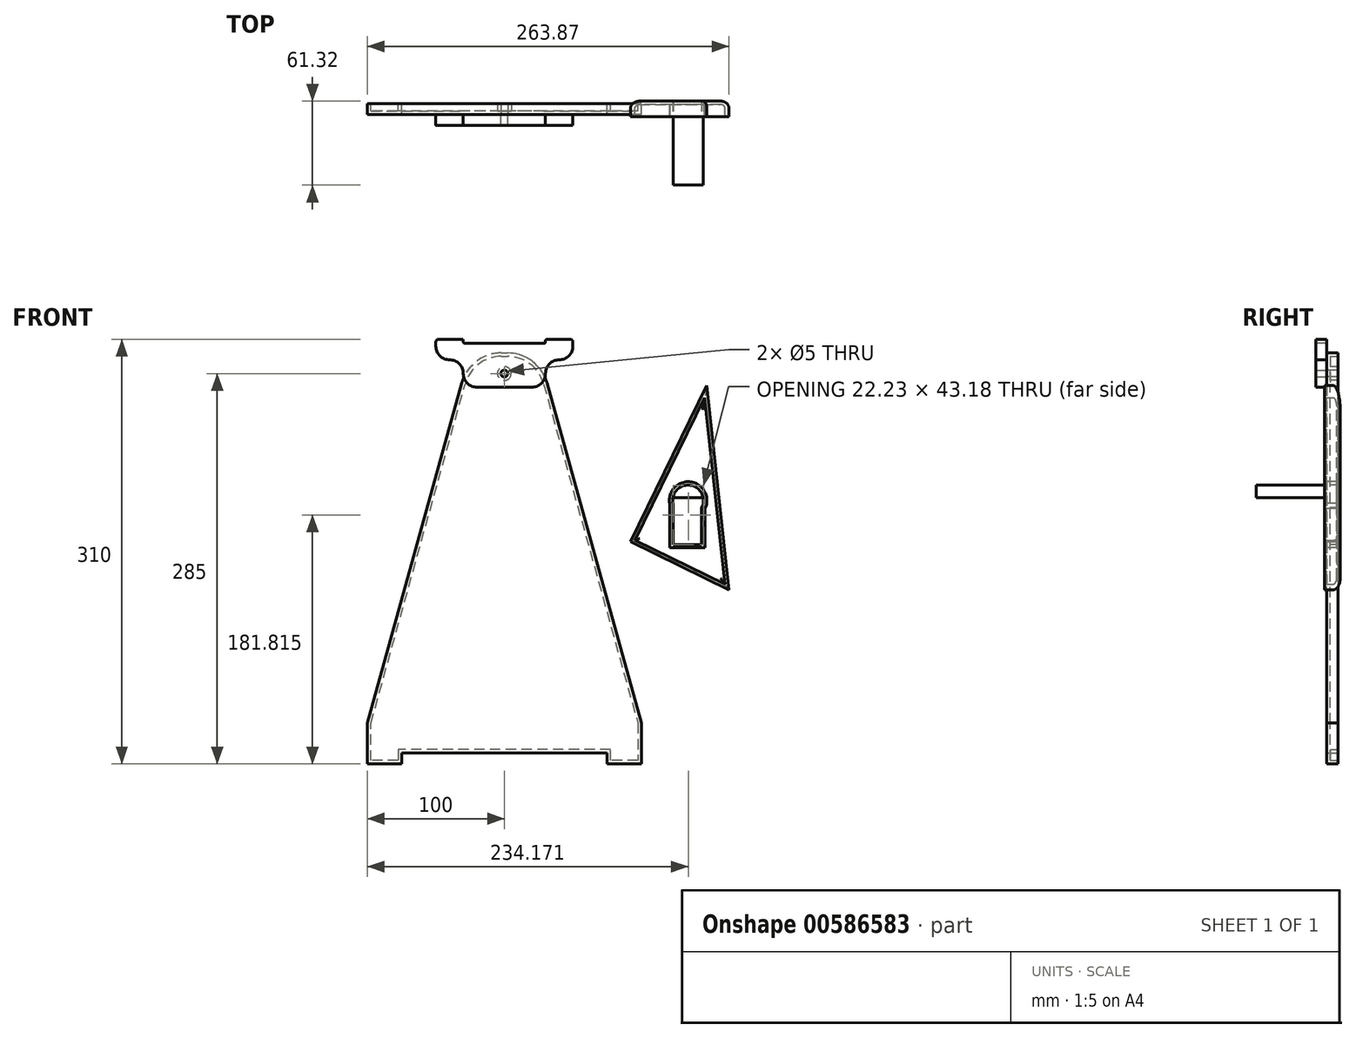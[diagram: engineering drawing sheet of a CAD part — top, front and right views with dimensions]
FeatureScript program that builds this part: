
annotation { "Feature Type Name" : "Feature", "Feature Type Description" : "" }
export const myFeature = defineFeature(function(context is Context, id is Id, definition is map)
    precondition{}
    {
        {
            var Q0;
            Q0=qCreatedBy(makeId("Front.planeOp"),FACE);
            var sketch = newSketch(context, id + "F0", { "sketchPlane" : qUnion([Q0])});
            skLineSegment(sketch, "E0", {"start": v(-25, 0) * mm, "end": v(25, 0) * mm});
            skLineSegment(sketch, "E1", {"start": v(25, 0) * mm, "end": v(100, -270) * mm});
            skLineSegment(sketch, "E2", {"start": v(100, -270) * mm, "end": v(100, -300) * mm});
            skLineSegment(sketch, "E3", {"start": v(100, -300) * mm, "end": v(75, -300) * mm});
            skLineSegment(sketch, "E4", {"start": v(75, -300) * mm, "end": v(75, -292) * mm});
            skLineSegment(sketch, "E5", {"start": v(75, -292) * mm, "end": v(-75, -292) * mm});
            skLineSegment(sketch, "E6", {"start": v(-75, -292) * mm, "end": v(-75, -300) * mm});
            skLineSegment(sketch, "E7", {"start": v(-75, -300) * mm, "end": v(-100, -300) * mm});
            skLineSegment(sketch, "E8", {"start": v(-100, -300) * mm, "end": v(-100, -270) * mm});
            skLineSegment(sketch, "E9", {"start": v(-100, -270) * mm, "end": v(-25, 0) * mm});
            skSolve(sketch);
        }
        {
            var Q0;
            Q0=makeQuery(id+"F0.imprint","IMPRINT",FACE,{"disambiguationData":[TD([[makeQuery(id+"F0.imprint","IMPRINT",EDGE,{"derivedFrom":sQuery(id+"F0.wireOp",EDGE,"E0")}),-1.0]])]});
            extrude(context, id + "F1", {"entities" : qUnion([Q0]), "endBound" : BoundingType.SYMMETRIC, "depth" : 8 * mm, "offsetDistance" : 25 * mm});
        }
        {
            var Q0;
            Q0=makeQuery(id+"F1.opExtrude","SWEPT_EDGE",EDGE,{"disambiguationData":[OSD([sQuery(id+"F0.wireOp",EDGE,"E0"),sQuery(id+"F0.wireOp",EDGE,"E9")])]});
            var Q1;
            Q1=makeQuery(id+"F1.opExtrude","SWEPT_EDGE",EDGE,{"disambiguationData":[OSD([sQuery(id+"F0.wireOp",EDGE,"E0"),sQuery(id+"F0.wireOp",EDGE,"E1")])]});
            fillet(context, id + "F2", {"entities" : qUnion([Q0, Q1]), "radius" : 30 * mm, "tangentPropagation" : true, "allowEdgeOverflow" : false});
        }
        {
            var Q0;
            Q0=makeQuery(id+"F1.opExtrude","CAP_FACE",FACE,{"disambiguationData":[OSD([sQuery(id+"F0.wireOp",EDGE,"E0"),sQuery(id+"F0.wireOp",EDGE,"E1"),sQuery(id+"F0.wireOp",EDGE,"E2"),sQuery(id+"F0.wireOp",EDGE,"E3"),sQuery(id+"F0.wireOp",EDGE,"E4"),sQuery(id+"F0.wireOp",EDGE,"E5"),sQuery(id+"F0.wireOp",EDGE,"E6"),sQuery(id+"F0.wireOp",EDGE,"E7"),sQuery(id+"F0.wireOp",EDGE,"E8"),sQuery(id+"F0.wireOp",EDGE,"E9")])],"isStart":false});
            var sketch = newSketch(context, id + "F3", { "sketchPlane" : qUnion([Q0])});
            skCircle(sketch, "E10", {"center": v(0, -15) * mm, "radius": 2.5 * mm});
            skSolve(sketch);
        }
        {
            var Q0;
            Q0=makeQuery(id+"F3.imprint","IMPRINT",FACE,{"disambiguationData":[TD([[makeQuery(id+"F3.imprint","IMPRINT",EDGE,{"derivedFrom":sQuery(id+"F3.wireOp",EDGE,"E10")}),1.0]])]});
            extrude(context, id + "F4", {"entities" : qUnion([Q0]), "operationType" : NewBodyOperationType.REMOVE, "endBound" : BoundingType.THROUGH_ALL, "oppositeDirection" : true, "depth" : 25 * mm, "offsetDistance" : 25 * mm});
        }
        {
            var Q0;
            Q0=makeQuery(id+"F1.opExtrude","CAP_FACE",FACE,{"disambiguationData":[OSD([sQuery(id+"F0.wireOp",EDGE,"E0"),sQuery(id+"F0.wireOp",EDGE,"E1"),sQuery(id+"F0.wireOp",EDGE,"E2"),sQuery(id+"F0.wireOp",EDGE,"E3"),sQuery(id+"F0.wireOp",EDGE,"E4"),sQuery(id+"F0.wireOp",EDGE,"E5"),sQuery(id+"F0.wireOp",EDGE,"E6"),sQuery(id+"F0.wireOp",EDGE,"E7"),sQuery(id+"F0.wireOp",EDGE,"E8"),sQuery(id+"F0.wireOp",EDGE,"E9")])],"isStart":false});
            var sketch = newSketch(context, id + "F5", { "sketchPlane" : qUnion([Q0])});
            skLineSegment(sketch, "E11", {"start": v(-50, 10) * mm, "end": v(50, 10) * mm});
            skLineSegment(sketch, "E12", {"start": v(50, 10) * mm, "end": v(50, -5) * mm});
            skLineSegment(sketch, "E13", {"start": v(50, -5) * mm, "end": v(30, -5) * mm});
            skLineSegment(sketch, "E14", {"start": v(30, -5) * mm, "end": v(30, -25) * mm});
            skLineSegment(sketch, "E15", {"start": v(30, -25) * mm, "end": v(-30, -25) * mm});
            skLineSegment(sketch, "E16", {"start": v(-30, -25) * mm, "end": v(-30, -5) * mm});
            skLineSegment(sketch, "E17", {"start": v(-30, -5) * mm, "end": v(-50, -5) * mm});
            skLineSegment(sketch, "E18", {"start": v(-50, -5) * mm, "end": v(-50, 10) * mm});
            skSolve(sketch);
        }
        {
            var Q0;
            Q0 = qSketchRegion(id + "F5", true);
            extrude(context, id + "F6", {"entities" : qUnion([Q0]), "depth" : 8 * mm, "offsetDistance" : 25 * mm});
        }
        {
            var Q0;
            Q0=makeQuery(id+"F6.opExtrude","SWEPT_EDGE",EDGE,{"disambiguationData":[OSD([sQuery(id+"F5.wireOp",EDGE,"E11"),sQuery(id+"F5.wireOp",EDGE,"E18")])]});
            var Q1;
            Q1=makeQuery(id+"F6.opExtrude","SWEPT_EDGE",EDGE,{"disambiguationData":[OSD([sQuery(id+"F5.wireOp",EDGE,"E11"),sQuery(id+"F5.wireOp",EDGE,"E12")])]});
            fillet(context, id + "F7", {"entities" : qUnion([Q0, Q1]), "radius" : 2 * mm, "tangentPropagation" : true, "allowEdgeOverflow" : false});
        }
        {
            var Q0;
            Q0=makeQuery(id+"F6.opExtrude","SWEPT_EDGE",EDGE,{"disambiguationData":[OSD([sQuery(id+"F5.wireOp",EDGE,"E13"),sQuery(id+"F5.wireOp",EDGE,"E14")])]});
            var Q1;
            Q1=makeQuery(id+"F6.opExtrude","SWEPT_EDGE",EDGE,{"disambiguationData":[OSD([sQuery(id+"F5.wireOp",EDGE,"E14"),sQuery(id+"F5.wireOp",EDGE,"E15")])]});
            var Q2;
            Q2=makeQuery(id+"F6.opExtrude","SWEPT_EDGE",EDGE,{"disambiguationData":[OSD([sQuery(id+"F5.wireOp",EDGE,"E15"),sQuery(id+"F5.wireOp",EDGE,"E16")])]});
            var Q3;
            Q3=makeQuery(id+"F6.opExtrude","SWEPT_EDGE",EDGE,{"disambiguationData":[OSD([sQuery(id+"F5.wireOp",EDGE,"E16"),sQuery(id+"F5.wireOp",EDGE,"E17")])]});
            var Q4;
            Q4=makeQuery(id+"F6.opExtrude","SWEPT_EDGE",EDGE,{"disambiguationData":[OSD([sQuery(id+"F5.wireOp",EDGE,"E17"),sQuery(id+"F5.wireOp",EDGE,"E18")])]});
            var Q5;
            Q5=makeQuery(id+"F6.opExtrude","SWEPT_EDGE",EDGE,{"disambiguationData":[OSD([sQuery(id+"F5.wireOp",EDGE,"E12"),sQuery(id+"F5.wireOp",EDGE,"E13")])]});
            fillet(context, id + "F8", {"entities" : qUnion([Q0, Q1, Q2, Q3, Q4, Q5]), "radius" : 10 * mm, "tangentPropagation" : true, "allowEdgeOverflow" : false});
        }
        {
            var Q0;
            Q0=makeQuery(id+"F6.opExtrude","CAP_FACE",FACE,{"disambiguationData":[OSD([sQuery(id+"F5.wireOp",EDGE,"E11"),sQuery(id+"F5.wireOp",EDGE,"E12"),sQuery(id+"F5.wireOp",EDGE,"E13"),sQuery(id+"F5.wireOp",EDGE,"E14"),sQuery(id+"F5.wireOp",EDGE,"E15"),sQuery(id+"F5.wireOp",EDGE,"E16"),sQuery(id+"F5.wireOp",EDGE,"E17"),sQuery(id+"F5.wireOp",EDGE,"E18")])],"isStart":false});
            var sketch = newSketch(context, id + "F9", { "sketchPlane" : qUnion([Q0])});
            skLineSegment(sketch, "E19.bottom", {"start": v(-30, 10) * mm, "end": v(30, 10) * mm});
            skLineSegment(sketch, "E19.top", {"start": v(-30, 7) * mm, "end": v(30, 7) * mm});
            skLineSegment(sketch, "E19.left", {"start": v(-30, 10) * mm, "end": v(-30, 7) * mm});
            skLineSegment(sketch, "E19.right", {"start": v(30, 10) * mm, "end": v(30, 7) * mm});
            skSolve(sketch);
        }
        {
            var Q0;
            Q0=makeQuery(id+"F9.imprint","IMPRINT",FACE,{"disambiguationData":[TD([[makeQuery(id+"F9.imprint","IMPRINT",EDGE,{"derivedFrom":sQuery(id+"F9.wireOp",EDGE,"E19.bottom")}),-1.0]])]});
            extrude(context, id + "F10", {"entities" : qUnion([Q0]), "operationType" : NewBodyOperationType.REMOVE, "endBound" : BoundingType.UP_TO_NEXT, "oppositeDirection" : true, "depth" : 25 * mm, "offsetDistance" : 25 * mm});
        }
        {
            var Q0;
            Q0=makeQuery(id+"F10.boolean.opBoolean","COPY",EDGE,{"derivedFrom":makeQuery(id+"F10.opExtrude","SWEPT_EDGE",EDGE,{"disambiguationData":[OSD([sQuery(id+"F5.wireOp",EDGE,"E11"),sQuery(id+"F9.wireOp",EDGE,"E19.bottom"),sQuery(id+"F9.wireOp",EDGE,"E19.left")])]})});
            var Q1;
            Q1=makeQuery(id+"F10.boolean.opBoolean","COPY",EDGE,{"derivedFrom":makeQuery(id+"F10.opExtrude","SWEPT_EDGE",EDGE,{"disambiguationData":[OSD([sQuery(id+"F9.wireOp",EDGE,"E19.top"),sQuery(id+"F9.wireOp",EDGE,"E19.left")])]})});
            var Q2;
            Q2=makeQuery(id+"F10.boolean.opBoolean","COPY",EDGE,{"derivedFrom":makeQuery(id+"F10.opExtrude","SWEPT_EDGE",EDGE,{"disambiguationData":[OSD([sQuery(id+"F5.wireOp",EDGE,"E11"),sQuery(id+"F9.wireOp",EDGE,"E19.bottom"),sQuery(id+"F9.wireOp",EDGE,"E19.right")])]})});
            var Q3;
            Q3=makeQuery(id+"F10.boolean.opBoolean","COPY",EDGE,{"derivedFrom":makeQuery(id+"F10.opExtrude","SWEPT_EDGE",EDGE,{"disambiguationData":[OSD([sQuery(id+"F9.wireOp",EDGE,"E19.top"),sQuery(id+"F9.wireOp",EDGE,"E19.right")])]})});
            fillet(context, id + "F11", {"entities" : qUnion([Q0, Q1, Q2, Q3]), "radius" : 1 * mm, "tangentPropagation" : true, "allowEdgeOverflow" : false});
        }
        {
            var Q0;
            Q0=makeQuery(id+"F6.opExtrude","CAP_FACE",FACE,{"disambiguationData":[OSD([sQuery(id+"F5.wireOp",EDGE,"E11"),sQuery(id+"F5.wireOp",EDGE,"E12"),sQuery(id+"F5.wireOp",EDGE,"E13"),sQuery(id+"F5.wireOp",EDGE,"E14"),sQuery(id+"F5.wireOp",EDGE,"E15"),sQuery(id+"F5.wireOp",EDGE,"E16"),sQuery(id+"F5.wireOp",EDGE,"E17"),sQuery(id+"F5.wireOp",EDGE,"E18")])],"isStart":true});
            var sketch = newSketch(context, id + "F12", { "sketchPlane" : qUnion([Q0])});
            skCircle(sketch, "E20.0", {"center": v(0, -15) * mm, "radius": 2.5 * mm});
            skSolve(sketch);
        }
        {
            var Q0;
            Q0 = qSketchRegion(id + "F12", true);
            extrude(context, id + "F13", {"entities" : qUnion([Q0]), "operationType" : NewBodyOperationType.REMOVE, "endBound" : BoundingType.UP_TO_NEXT, "oppositeDirection" : true, "depth" : 25 * mm, "offsetDistance" : 25 * mm});
        }
        {
            var Q0;
            Q0=qCreatedBy(makeId("Front.planeOp"),FACE);
            var sketch = newSketch(context, id + "F14", { "sketchPlane" : qUnion([Q0])});
            skLineSegment(sketch, "E21", {"start": v(92, -137.78) * mm, "end": v(147.78, -23.81) * mm});
            skLineSegment(sketch, "E22", {"start": v(147.78, -23.81) * mm, "end": v(163.87, -172.95) * mm});
            skLineSegment(sketch, "E23", {"start": v(163.87, -172.95) * mm, "end": v(92, -137.78) * mm});
            skSolve(sketch);
        }
        {
            var Q0;
            Q0=makeQuery(id+"F14.imprint","IMPRINT",FACE,{"disambiguationData":[TD([[makeQuery(id+"F14.imprint","IMPRINT",EDGE,{"derivedFrom":sQuery(id+"F14.wireOp",EDGE,"E21")}),-1.0]])]});
            extrude(context, id + "F15", {"entities" : qUnion([Q0]), "endBound" : BoundingType.SYMMETRIC, "depth" : 11.32 * mm, "offsetDistance" : 25 * mm});
        }
        {
            var Q0;
            Q0=makeQuery(id+"F15.opExtrude","CAP_FACE",FACE,{"disambiguationData":[OSD([sQuery(id+"F14.wireOp",EDGE,"E21"),sQuery(id+"F14.wireOp",EDGE,"E22"),sQuery(id+"F14.wireOp",EDGE,"E23")])],"isStart":false});
            var sketch = newSketch(context, id + "F16", { "sketchPlane" : qUnion([Q0])});
            skCircle(sketch, "E24", {"center": v(134.08, -107.67) * mm, "radius": 11.2 * mm});
            skLineSegment(sketch, "E25.bottom", {"start": v(123.06, -109.68) * mm, "end": v(144, -109.68) * mm});
            skLineSegment(sketch, "E25.top", {"start": v(123.06, -139.77) * mm, "end": v(144, -139.77) * mm});
            skLineSegment(sketch, "E25.left", {"start": v(123.06, -109.68) * mm, "end": v(123.06, -139.77) * mm});
            skLineSegment(sketch, "E25.right", {"start": v(144, -109.68) * mm, "end": v(144, -139.77) * mm});
            skSolve(sketch);
        }
        {
            var Q0;
            Q0 = qSketchRegion(id + "F16", true);
            extrude(context, id + "F17", {"entities" : qUnion([Q0]), "operationType" : NewBodyOperationType.REMOVE, "endBound" : BoundingType.THROUGH_ALL, "oppositeDirection" : true, "depth" : 25 * mm, "offsetDistance" : 25 * mm});
        }
        {
            var Q0;
            Q0=makeQuery(id+"F15.opExtrude","CAP_EDGE",EDGE,{"disambiguationData":[OSD([sQuery(id+"F14.wireOp",EDGE,"E22")])],"isStart":true});
            var Q1;
            Q1=makeQuery(id+"F15.opExtrude","CAP_EDGE",EDGE,{"disambiguationData":[OSD([sQuery(id+"F14.wireOp",EDGE,"E23")])],"isStart":true});
            var Q2;
            Q2=makeQuery(id+"F15.opExtrude","CAP_EDGE",EDGE,{"disambiguationData":[OSD([sQuery(id+"F14.wireOp",EDGE,"E21")])],"isStart":true});
            fillet(context, id + "F18", {"entities" : qUnion([Q0, Q1, Q2]), "radius" : 5 * mm, "tangentPropagation" : true, "allowEdgeOverflow" : false});
        }
        {
            var Q0;
            Q0=makeQuery(id+"F15.opExtrude","CAP_FACE",FACE,{"disambiguationData":[OSD([sQuery(id+"F14.wireOp",EDGE,"E21"),sQuery(id+"F14.wireOp",EDGE,"E22"),sQuery(id+"F14.wireOp",EDGE,"E23")])],"isStart":false});
            var sketch = newSketch(context, id + "F19", { "sketchPlane" : qUnion([Q0])});
            skLineSegment(sketch, "E26.bottom", {"start": v(123.06, -151.76) * mm, "end": v(150.38, -151.76) * mm});
            skLineSegment(sketch, "E26.top", {"start": v(123.06, -105.66) * mm, "end": v(150.38, -105.66) * mm});
            skLineSegment(sketch, "E26.left", {"start": v(123.06, -151.76) * mm, "end": v(123.06, -105.66) * mm});
            skLineSegment(sketch, "E26.right", {"start": v(150.38, -151.76) * mm, "end": v(150.38, -105.66) * mm});
            skPoint(sketch, "E26.middle", {"position": v(136.72, -128.71) * mm});
            skSolve(sketch);
        }
        {
            var Q0;
            {var subQ0=makeQuery(id+"F17.boolean.opBoolean","COPY",EDGE,{"derivedFrom":makeQuery(id+"F17.opExtrude","CAP_EDGE",EDGE,{"disambiguationData":[OSD([sQuery(id+"F16.wireOp",EDGE,"E25.top")])],"isStart":true})});Q0=makeQuery(id+"F19.imprint","IMPRINT",FACE,{"disambiguationData":[TD([[makeQuery(id+"F19.imprint","IMPRINT",EDGE,{"derivedFrom":subQ0}),1.0]])]});}
            var Q1;
            {var subQ0=sQuery(id+"F19.wireOp",EDGE,"E26.top");var subQ1=makeQuery(id+"F17.boolean.opBoolean","COPY",EDGE,{"derivedFrom":makeQuery(id+"F17.opExtrude","CAP_EDGE",EDGE,{"disambiguationData":[OSD([sQuery(id+"F16.wireOp",EDGE,"E24")])],"isStart":true})});var subQ3=makeQuery(id+"F19.imprint","INTERSECT",VERTEX,{"derivedFrom":[subQ1,subQ0]});Q1=makeQuery(id+"F19.imprint","IMPRINT",FACE,{"disambiguationData":[TD([[makeQuery(id+"F19.imprint","IMPRINT",EDGE,{"disambiguationData":[TD([[subQ3,1.0]])],"derivedFrom":subQ0}),1.0]])]});}
            var Q2;
            Q2=sQuery(id+"F19.wireOp",EDGE,"E26.bottom");
            var Q3;
            Q3=sQuery(id+"F19.wireOp",EDGE,"E26.right");
            extrude(context, id + "F20", {"entities" : qUnion([Q0, Q1]), "surfaceEntities" : qUnion([Q2, Q3]), "depth" : 50 * mm, "offsetDistance" : 25 * mm});
        }
        {
            var Q0;
            Q0=makeQuery(id+"F1.opExtrude","CAP_FACE",FACE,{"disambiguationData":[OSD([sQuery(id+"F0.wireOp",EDGE,"E0"),sQuery(id+"F0.wireOp",EDGE,"E1"),sQuery(id+"F0.wireOp",EDGE,"E2"),sQuery(id+"F0.wireOp",EDGE,"E3"),sQuery(id+"F0.wireOp",EDGE,"E4"),sQuery(id+"F0.wireOp",EDGE,"E5"),sQuery(id+"F0.wireOp",EDGE,"E6"),sQuery(id+"F0.wireOp",EDGE,"E7"),sQuery(id+"F0.wireOp",EDGE,"E8"),sQuery(id+"F0.wireOp",EDGE,"E9")])],"isStart":true});
            var Q1;
            Q1=makeQuery(id+"F15.opExtrude","CAP_FACE",FACE,{"disambiguationData":[OSD([sQuery(id+"F14.wireOp",EDGE,"E21"),sQuery(id+"F14.wireOp",EDGE,"E22"),sQuery(id+"F14.wireOp",EDGE,"E23")])],"isStart":false});
            shell(context, id + "F21", {"entities" : qUnion([Q0, Q1]), "thickness" : 2.5 * mm});
        }
    });
